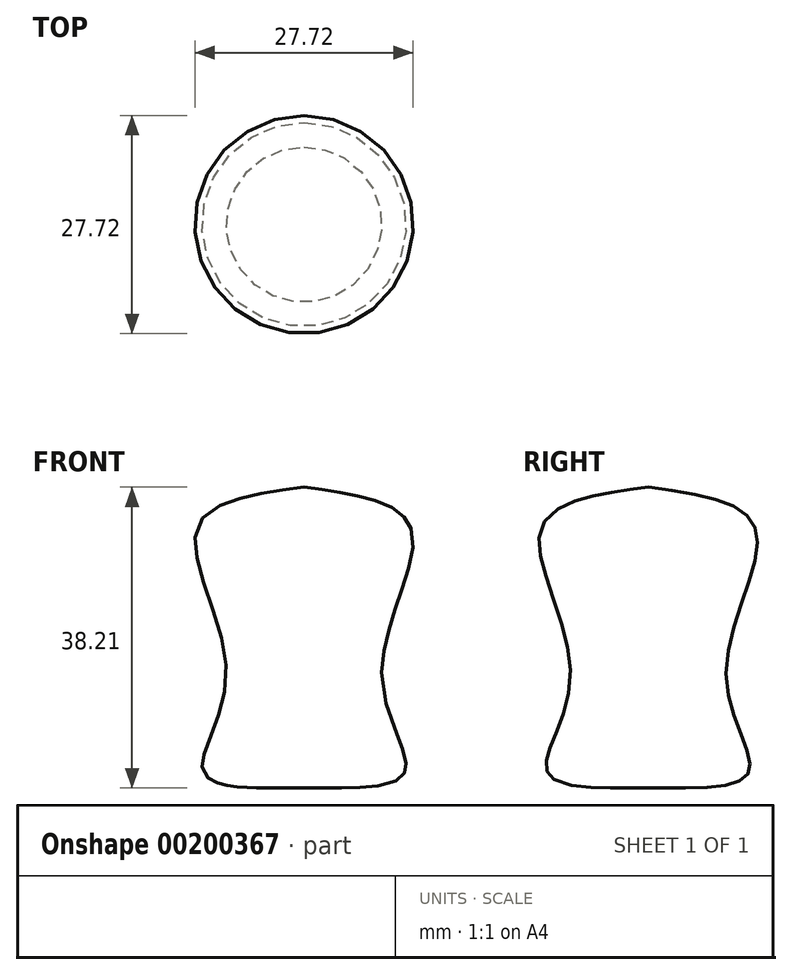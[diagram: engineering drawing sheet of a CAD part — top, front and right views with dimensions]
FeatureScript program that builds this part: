
annotation { "Feature Type Name" : "Feature", "Feature Type Description" : "" }
export const myFeature = defineFeature(function(context is Context, id is Id, definition is map)
    precondition{}
    {
        {
            var Q0;
            Q0=qCreatedBy(makeId("Right.planeOp"),FACE);
            var sketch = newSketch(context, id + "F0", { "sketchPlane" : qUnion([Q0])});
            skFitSpline(sketch, "E0", {"points": [v(0, 44.12) * mm, v(13.65, 38.8) * mm, v(9.87, 20.09) * mm, v(12.79, 7.9) * mm, v(0, 6) * mm], "startDerivative": vector(75.03, -9.96) * mm, "endDerivative": vector(-75.4, 2.34) * mm});
            skLineSegment(sketch, "E1", {"start": v(0, 44.12) * mm, "end": v(0, 6) * mm});
            skSolve(sketch);
        }
        {
            var Q0;
            Q0=makeQuery(id+"F0.imprint","IMPRINT",FACE,{"disambiguationData":[TD([[makeQuery(id+"F0.imprint","IMPRINT",EDGE,{"derivedFrom":sQuery(id+"F0.wireOp",EDGE,"E0")}),-1.0]])]});
            var Q1;
            Q1=sQuery(id+"F0.wireOp",EDGE,"E1");
            revolve(context, id + "F1", {"entities" : qUnion([Q0]), "axis" : qUnion([Q1]), "revolveType" : RevolveType.FULL});
        }
    });
